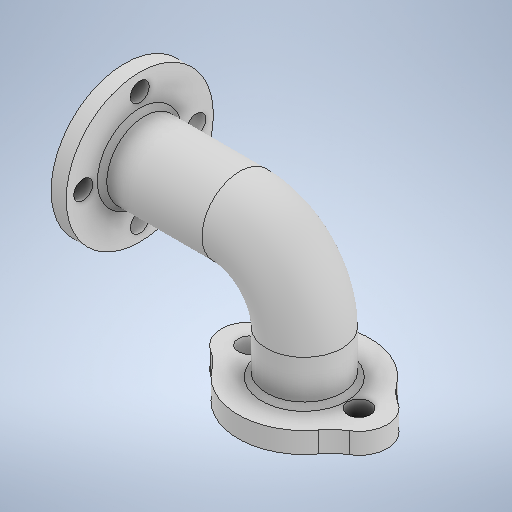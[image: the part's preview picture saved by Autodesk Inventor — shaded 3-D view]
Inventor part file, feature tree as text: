
AUTODESK INVENTOR PART (.ipt)
format: ipt  version: 2025.2 (Build 292293000, 293)  size: 707,584 bytes
history: native  units: in
note: dims shown in document units (in); Inventor stores cm internally (conversion verified against a paired STEP export)
features: sketch x19, extrude x3, chamfer x2, plane x1, sweep x1, shell x1, other x1
ambient origin geometry x8: Origin, YZ Plane, XZ Plane, XY Plane, X Axis, Y Axis, Z Axis, Center Point
bodies: Solid1 (feature_tree)
feature tree (28):
  sketch  "Sketch1"  dims[d7=-0.75in d13=2.2835in d15=1.378in]
  plane  "Work Plane1"
  sketch  "Sketch2"  dims[d19=0.2756in d20=3.0709in]
  sweep  "Sweep1"
  shell  "Shell1"  Thickness=1.378in
  sketch  "Sketch4"  dims[d24=0.3937in d25=1.1811in d26=1.5748in d28=360.0deg]
  sketch  "Sketch5"  dims[d30=0.315in d31=0.0in]
  sketch  "Sketch6"  dims[d32=0.0984in d33=0.0787in d34=45.0deg]
  sketch  "Sketch7"  dims[d35=2.7559in]
  sketch  "Sketch8"  dims[d36=1.0236in]
  sketch  "Sketch9"  dims[d38=0.4724in]
  sketch  "Sketch10"  dims[d39=1.1417in]
  sketch  "Sketch11"  dims[d41=1.1811in]
  sketch  "Sketch12"  dims[d42=1.1417in]
  sketch  "Sketch13"  dims[d43=0.4331in d44=0.0in]
  sketch  "Sketch14"  dims[d45=0.0984in d46=0.0787in d47=45.0deg]
  sketch  "Sketch15"  dims[d48=0.0in]
  extrude  "Extrusion1"  TaperAngle=0.0deg  [1 undecoded]
  extrude  "Extrusion2"  Depth=3.0709in
  chamfer  "Chamfer1"  Distance=0.315in
  extrude  "Extrusion3"  Depth=1.1811in
  chamfer  "Chamfer2"  Distance=1.5748in Angle=360.0deg
  other  "Image1"
  sketch  "Sketch3"  dims[d21=1.0236in d22=0.315in d23=0.0in]
  sketch  "Sketch16"
  sketch  "Sketch17"
  sketch  "Sketch Circular Pattern1"  dims[d16=1.5748in d17=0.0in d18=0.0in]
  sketch  "Sketch18"
note: 1 required parameter value undecoded (feature->parameter linkage not recoverable at this tier; creation-order binding heuristic only, values carry confidence <= 0.55)
